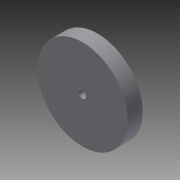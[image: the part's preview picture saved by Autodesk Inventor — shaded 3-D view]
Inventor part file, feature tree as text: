
AUTODESK INVENTOR PART (.ipt)
format: ipt  version: 2014 (Build 180170000, 170)  size: 75,776 bytes
history: native  units: in
note: dims shown in document units (in); Inventor stores cm internally (conversion verified against a paired STEP export)
features: extrude x1, sketch x1
ambient origin geometry x8: Origin, YZ Plane, XZ Plane, XY Plane, X Axis, Y Axis, Z Axis, Center Point
bodies: Solid1 (feature_tree)
feature tree (2):
  extrude  "Extrusion1"  Depth=1.0in
  sketch  "Sketch1"  dims[d0=6.0in d1=0.499in d2=1.0in d3=0.0in]
